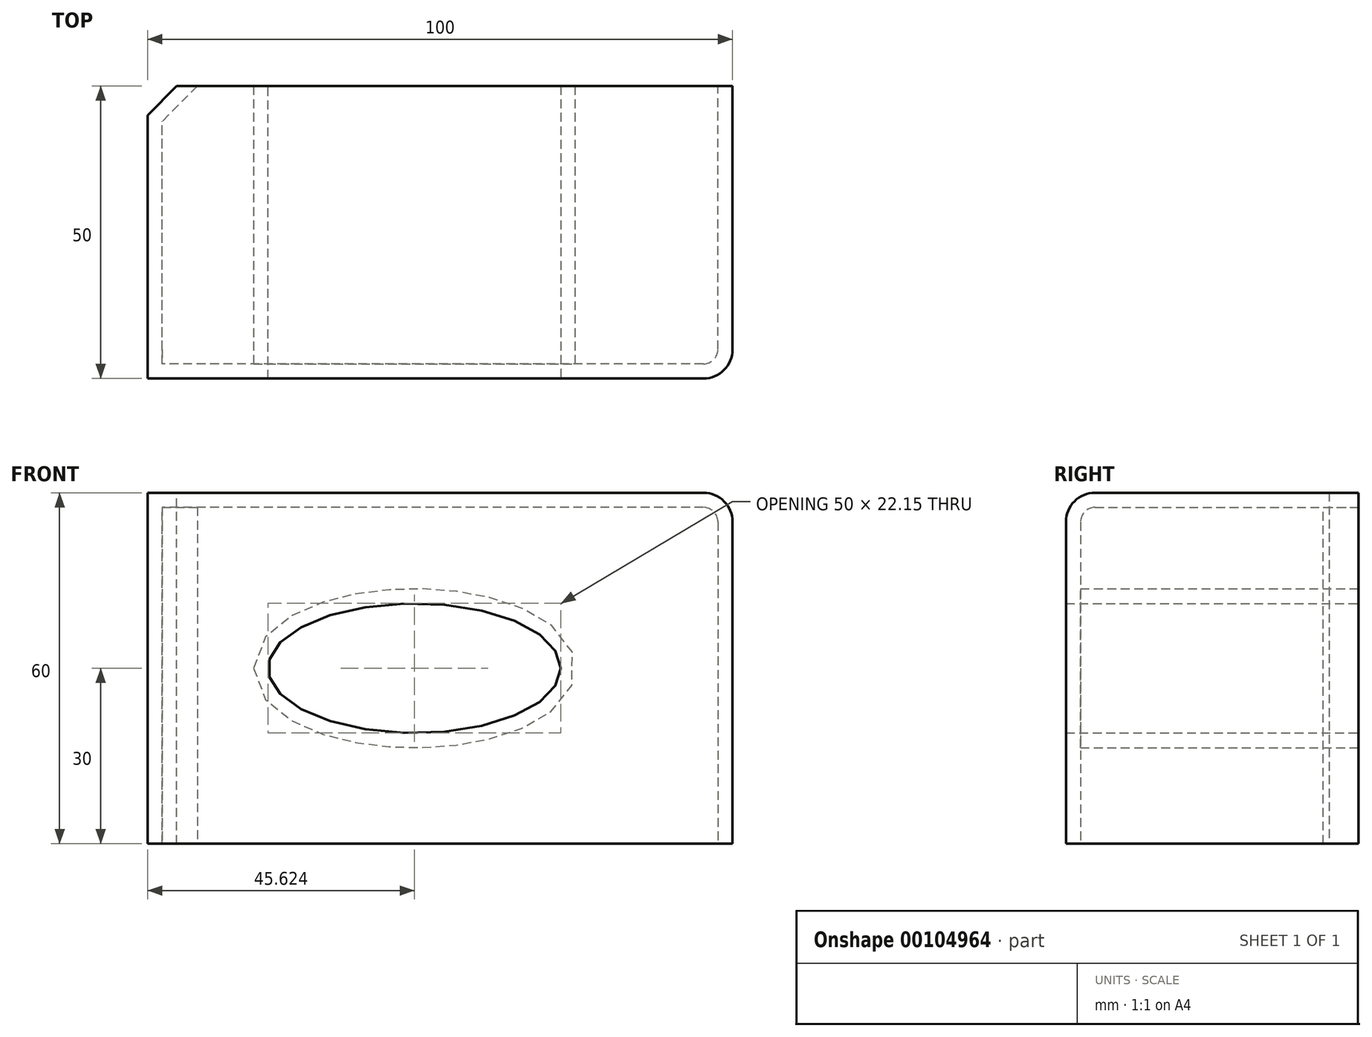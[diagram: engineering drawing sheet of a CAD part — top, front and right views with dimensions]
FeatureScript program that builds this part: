
annotation { "Feature Type Name" : "Feature", "Feature Type Description" : "" }
export const myFeature = defineFeature(function(context is Context, id is Id, definition is map)
    precondition{}
    {
        {
            var Q0;
            Q0=qCreatedBy(makeId("Front.planeOp"),FACE);
            var sketch = newSketch(context, id + "F0", { "sketchPlane" : qUnion([Q0])});
            skLineSegment(sketch, "E0.bottom", {"start": v(50, 30) * mm, "end": v(-50, 30) * mm});
            skLineSegment(sketch, "E0.top", {"start": v(50, -30) * mm, "end": v(-50, -30) * mm});
            skLineSegment(sketch, "E0.left", {"start": v(50, 30) * mm, "end": v(50, -30) * mm});
            skLineSegment(sketch, "E0.right", {"start": v(-50, 30) * mm, "end": v(-50, -30) * mm});
            skPoint(sketch, "E0.middle", {"position": v(0, 0) * mm});
            skSolve(sketch);
        }
        {
            var Q0;
            Q0 = qSketchRegion(id + "F0", true);
            extrude(context, id + "F1", {"entities" : qUnion([Q0]), "depth" : 50 * mm});
        }
        {
            var Q0;
            Q0=makeQuery(id+"F1.opExtrude","CAP_EDGE",EDGE,{"disambiguationData":[OSD([sQuery(id+"F0.wireOp",EDGE,"E0.bottom")])],"isStart":false});
            var Q1;
            Q1=makeQuery(id+"F1.opExtrude","SWEPT_EDGE",EDGE,{"disambiguationData":[OSD([sQuery(id+"F0.wireOp",EDGE,"E0.bottom"),sQuery(id+"F0.wireOp",EDGE,"E0.left")])]});
            var Q2;
            Q2=makeQuery(id+"F1.opExtrude","CAP_EDGE",EDGE,{"disambiguationData":[OSD([sQuery(id+"F0.wireOp",EDGE,"E0.left")])],"isStart":false});
            fillet(context, id + "F2", {"entities" : qUnion([Q0, Q1, Q2]), "radius" : 5 * mm, "tangentPropagation" : true, "allowEdgeOverflow" : false});
        }
        {
            var Q0;
            Q0=makeQuery(id+"F1.opExtrude","CAP_EDGE",EDGE,{"disambiguationData":[OSD([sQuery(id+"F0.wireOp",EDGE,"E0.right")])],"isStart":true});
            chamfer(context, id + "F3", {"entities" : qUnion([Q0]), "width" : 5 * mm, "tangentPropagation" : true});
        }
        {
            var Q0;
            Q0=makeQuery(id+"F1.opExtrude","CAP_FACE",FACE,{"disambiguationData":[OSD([sQuery(id+"F0.wireOp",EDGE,"E0.bottom"),sQuery(id+"F0.wireOp",EDGE,"E0.top"),sQuery(id+"F0.wireOp",EDGE,"E0.left"),sQuery(id+"F0.wireOp",EDGE,"E0.right")])],"isStart":false});
            var sketch = newSketch(context, id + "F4", { "sketchPlane" : qUnion([Q0])});
            skEllipse(sketch, "E1", {"center": v(-4.38, 0) * mm, "majorRadius": 25 * mm, "minorRadius": 11.08 * mm, "majorAxis": v(1, 0)});
            skSolve(sketch);
        }
        {
            var Q0;
            Q0 = qSketchRegion(id + "F4", true);
            extrude(context, id + "F5", {"entities" : qUnion([Q0]), "operationType" : NewBodyOperationType.REMOVE, "endBound" : BoundingType.THROUGH_ALL, "oppositeDirection" : true, "depth" : 25 * mm});
        }
        {
            var Q0;
            Q0=makeQuery(id+"F1.opExtrude","CAP_FACE",FACE,{"disambiguationData":[OSD([sQuery(id+"F0.wireOp",EDGE,"E0.bottom"),sQuery(id+"F0.wireOp",EDGE,"E0.top"),sQuery(id+"F0.wireOp",EDGE,"E0.left"),sQuery(id+"F0.wireOp",EDGE,"E0.right")])],"isStart":true});
            var Q1;
            Q1=makeQuery(id+"F1.opExtrude","SWEPT_FACE",FACE,{"disambiguationData":[OSD([sQuery(id+"F0.wireOp",EDGE,"E0.top")])]});
            shell(context, id + "F6", {"entities" : qUnion([Q0, Q1]), "thickness" : 2.5 * mm});
        }
    });
